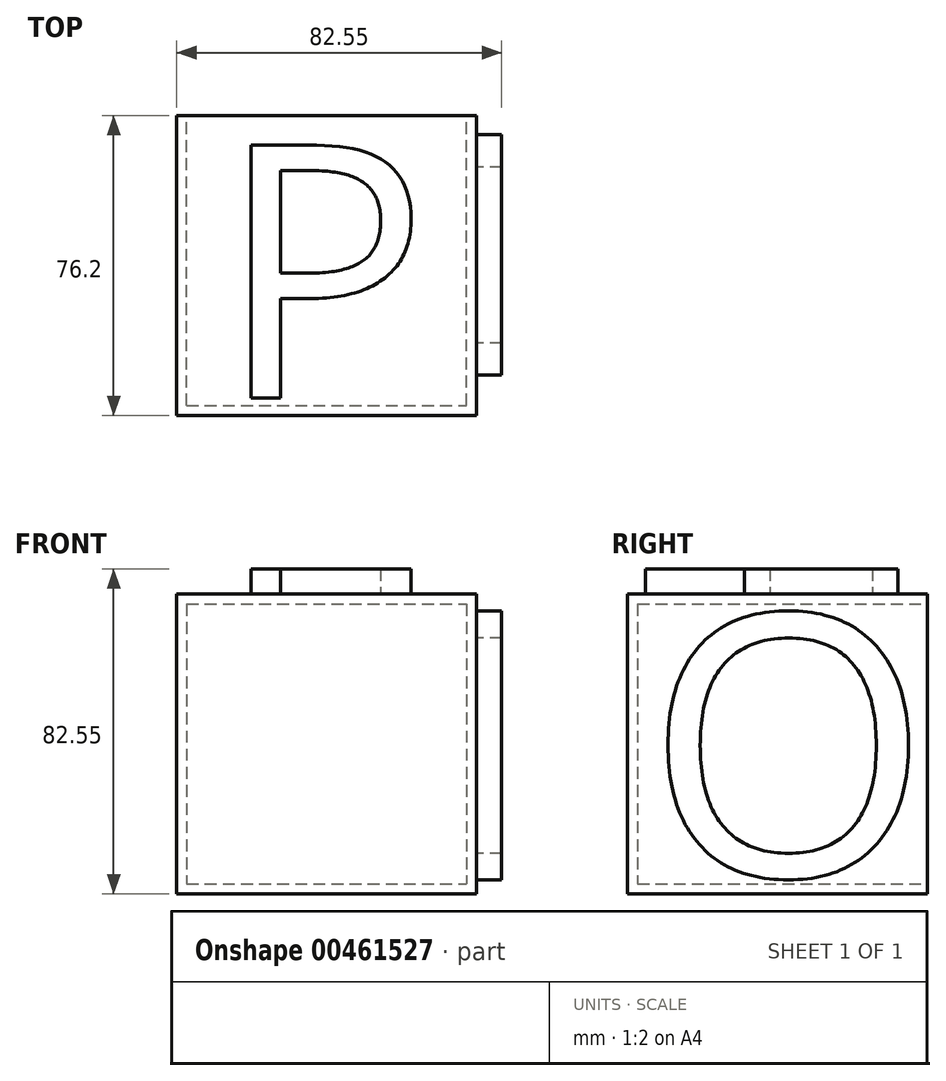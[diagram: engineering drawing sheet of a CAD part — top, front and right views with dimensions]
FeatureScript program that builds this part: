
annotation { "Feature Type Name" : "Feature", "Feature Type Description" : "" }
export const myFeature = defineFeature(function(context is Context, id is Id, definition is map)
    precondition{}
    {
        {
            var Q0;
            Q0=qCreatedBy(makeId("Front.planeOp"),FACE);
            var sketch = newSketch(context, id + "F0", { "sketchPlane" : qUnion([Q0])});
            skLineSegment(sketch, "E0.bottom", {"start": v(-40.85, 31.47) * mm, "end": v(35.35, 31.47) * mm});
            skLineSegment(sketch, "E0.top", {"start": v(-40.85, -44.73) * mm, "end": v(35.35, -44.73) * mm});
            skLineSegment(sketch, "E0.left", {"start": v(-40.85, 31.47) * mm, "end": v(-40.85, -44.73) * mm});
            skLineSegment(sketch, "E0.right", {"start": v(35.35, 31.47) * mm, "end": v(35.35, -44.73) * mm});
            skSolve(sketch);
        }
        {
            var Q0;
            Q0=makeQuery(id+"F0.imprint","IMPRINT",FACE,{"disambiguationData":[TD([[makeQuery(id+"F0.imprint","IMPRINT",EDGE,{"derivedFrom":sQuery(id+"F0.wireOp",EDGE,"E0.bottom")}),-1.0]])]});
            extrude(context, id + "F1", {"entities" : qUnion([Q0]), "depth" : 76.2 * mm});
        }
        {
            var Q0;
            Q0=makeQuery(id+"F1.opExtrude","SWEPT_FACE",FACE,{"disambiguationData":[OSD([sQuery(id+"F0.wireOp",EDGE,"E0.bottom")])]});
            var sketch = newSketch(context, id + "F2", { "sketchPlane" : qUnion([Q0])});
            skSolve(sketch);
        }
        {
            var Q0;
            Q0=makeQuery(id+"F1.opExtrude","CAP_FACE",FACE,{"disambiguationData":[OSD([sQuery(id+"F0.wireOp",EDGE,"E0.bottom"),sQuery(id+"F0.wireOp",EDGE,"E0.top"),sQuery(id+"F0.wireOp",EDGE,"E0.left"),sQuery(id+"F0.wireOp",EDGE,"E0.right")])],"isStart":true});
            shell(context, id + "F3", {"entities" : qUnion([Q0]), "thickness" : 2.54 * mm});
        }
        {
            var Q0;
            {var subQ0=sQuery(id+"F0.wireOp",EDGE,"E0.bottom");Q0=makeQuery(id+"F2.imprint","IMPRINT",FACE,{"disambiguationData":[TD([[makeQuery(id+"F2.imprint","IMPRINT",EDGE,{"derivedFrom":makeQuery(id+"F1.opExtrude","CAP_EDGE",EDGE,{"disambiguationData":[OSD([subQ0])],"isStart":true})}),-1.0]])]});}
            var sketch = newSketch(context, id + "F4", { "sketchPlane" : qUnion([Q0])});
            skText(sketch, "E1", { "text": "P", "fontName": "OpenSans-Regular.ttf"});
            const initialGuessF4  = {"E1": [-0.0308, -0.0717, 1, 0, 0.0647]};
            skSetInitialGuess(sketch, initialGuessF4);
            skSolve(sketch);
        }
        {
            var Q0;
            Q0 = qSketchRegion(id + "F4", true);
            var Q1;
            Q1 = qSketchRegion(id + "FE5zmXdMPlErjyX_1", true);
            extrude(context, id + "F5", {"entities" : qUnion([Q0, Q1]), "operationType" : NewBodyOperationType.ADD, "depth" : 6.35 * mm, "offsetDistance" : 25.4 * mm});
        }
        {
            var Q0;
            Q0=makeQuery(id+"F1.opExtrude","SWEPT_FACE",FACE,{"disambiguationData":[OSD([sQuery(id+"F0.wireOp",EDGE,"E0.right")])]});
            var sketch = newSketch(context, id + "F6", { "sketchPlane" : qUnion([Q0])});
            skText(sketch, "E2", { "text": "O", "fontName": "OpenSans-Regular.ttf"});
            const initialGuessF6  = {"E2": [-0.0716, -0.04025, 1, 0, 0.06695]};
            skSetInitialGuess(sketch, initialGuessF6);
            skSolve(sketch);
        }
        {
            var Q0;
            Q0 = qSketchRegion(id + "F6", true);
            extrude(context, id + "F7", {"entities" : qUnion([Q0]), "operationType" : NewBodyOperationType.ADD, "depth" : 6.35 * mm, "offsetDistance" : 25.4 * mm});
        }
    });
